# Revit family: NLRS_52_GM_HWA_vierkant_MR
name_source: partatom
category: Generic Models
revit_build: Autodesk Revit 2017 (Build: 20190507_1515(x64)
units: mm (PartAtom-declared; Revit-internal decimal feet)

## family parameters
Always vertical = Yes
Can host rebar = No
Cut with Voids When Loaded = No
Part Type = Normal
Room Calculation Point = No
Round Connector Dimension = Use Diameter
Shared = No
Work Plane-Based = No

## types (2) — shared parameters
Description = Hemelwater afvoer
Manufacturer = Meilof Riks bv
NLRS_C_diameter = 100 mm  [stored 0.328084 ft]
NLRS_C_hoek = 42.00°
Type Comments = HWA
a2 = 50 mm  [stored 0.164042 ft]

## per-type parameters (varying)
| type | Model | NLRS_C_Materiaal | URL |
| HWA 80 |  | RAL 9010 | https://www.meilofriks.nl |
| HWA 100 | HWA 100 | RAL 7016 |  |

note: [stored X ft] marks values corroborated as IEEE doubles in the binary element streams (Revit-internal decimal feet)

## geometry (parser evidence)
native form markers: Sweep x9
no freeform markers — native parametric forms only
